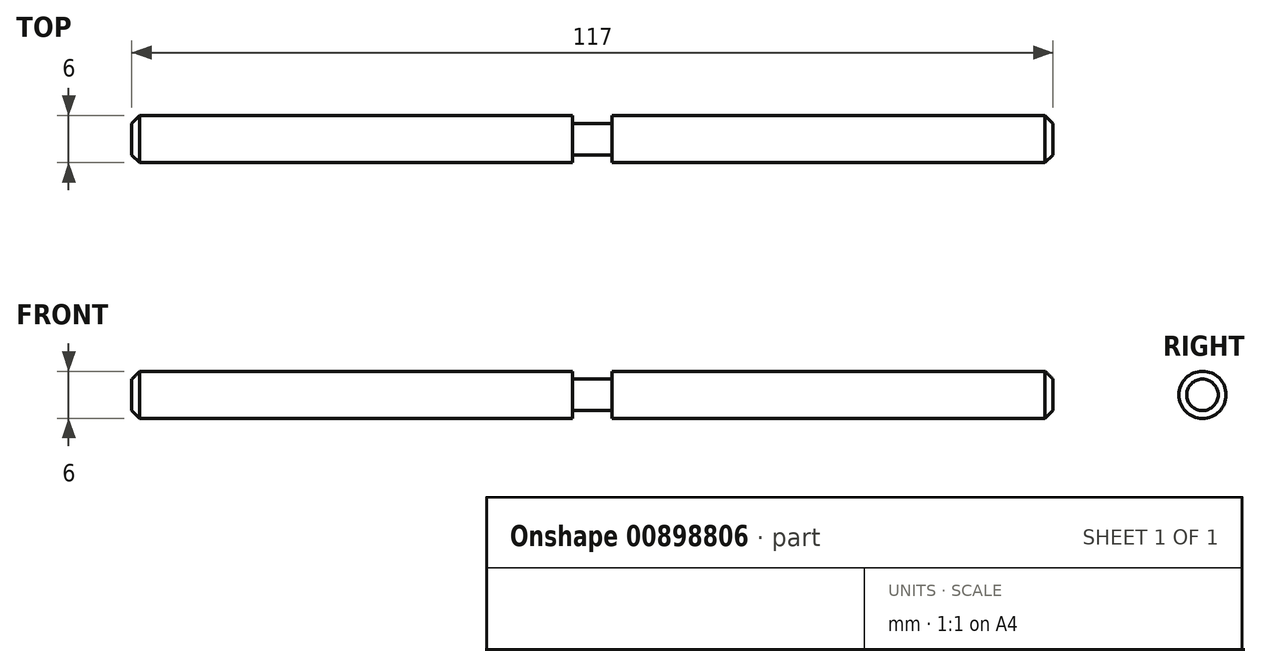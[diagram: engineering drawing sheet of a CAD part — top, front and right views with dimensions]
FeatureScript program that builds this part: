
annotation { "Feature Type Name" : "Feature", "Feature Type Description" : "" }
export const myFeature = defineFeature(function(context is Context, id is Id, definition is map)
    precondition{}
    {
        {
            var Q0;
            Q0=qCreatedBy(makeId("Top.planeOp"),FACE);
            var sketch = newSketch(context, id + "F0", { "sketchPlane" : qUnion([Q0])});
            skLineSegment(sketch, "E0.bottom", {"start": v(0, 0) * mm, "end": v(117, 0) * mm});
            skLineSegment(sketch, "E0.top", {"start": v(1, 3) * mm, "end": v(56, 3) * mm});
            skLineSegment(sketch, "E0.left", {"start": v(0, 0) * mm, "end": v(0, 2) * mm});
            skLineSegment(sketch, "E0.right", {"start": v(117, 0) * mm, "end": v(117, 2) * mm});
            skLineSegment(sketch, "E1", {"start": v(0, 2) * mm, "end": v(1, 3) * mm});
            skPoint(sketch, "E2.orphan", {"position": v(0, 3) * mm});
            skLineSegment(sketch, "E3.MirrorCS", {"start": v(117, 2) * mm, "end": v(116, 3) * mm});
            skLineSegment(sketch, "E4", {"start": v(56, 3) * mm, "end": v(56, 2) * mm});
            skLineSegment(sketch, "E5", {"start": v(61, 3) * mm, "end": v(61, 2) * mm});
            skLineSegment(sketch, "E6", {"start": v(56, 2) * mm, "end": v(61, 2) * mm});
            skPoint(sketch, "E7.orphan", {"position": v(58.5, 0) * mm});
            skLineSegment(sketch, "E8.trimOffspring", {"start": v(61, 3) * mm, "end": v(116, 3) * mm});
            skSolve(sketch);
        }
        {
            var Q0;
            Q0 = qSketchRegion(id + "F0", true);
            var Q1;
            Q1=sQuery(id+"F0.wireOp",EDGE,"E0.bottom");
            revolve(context, id + "F1", {"surfaceOperationType" : NewSurfaceOperationType.NEW, "entities" : qUnion([Q0]), "axis" : qUnion([Q1]), "revolveType" : RevolveType.FULL});
        }
    });
